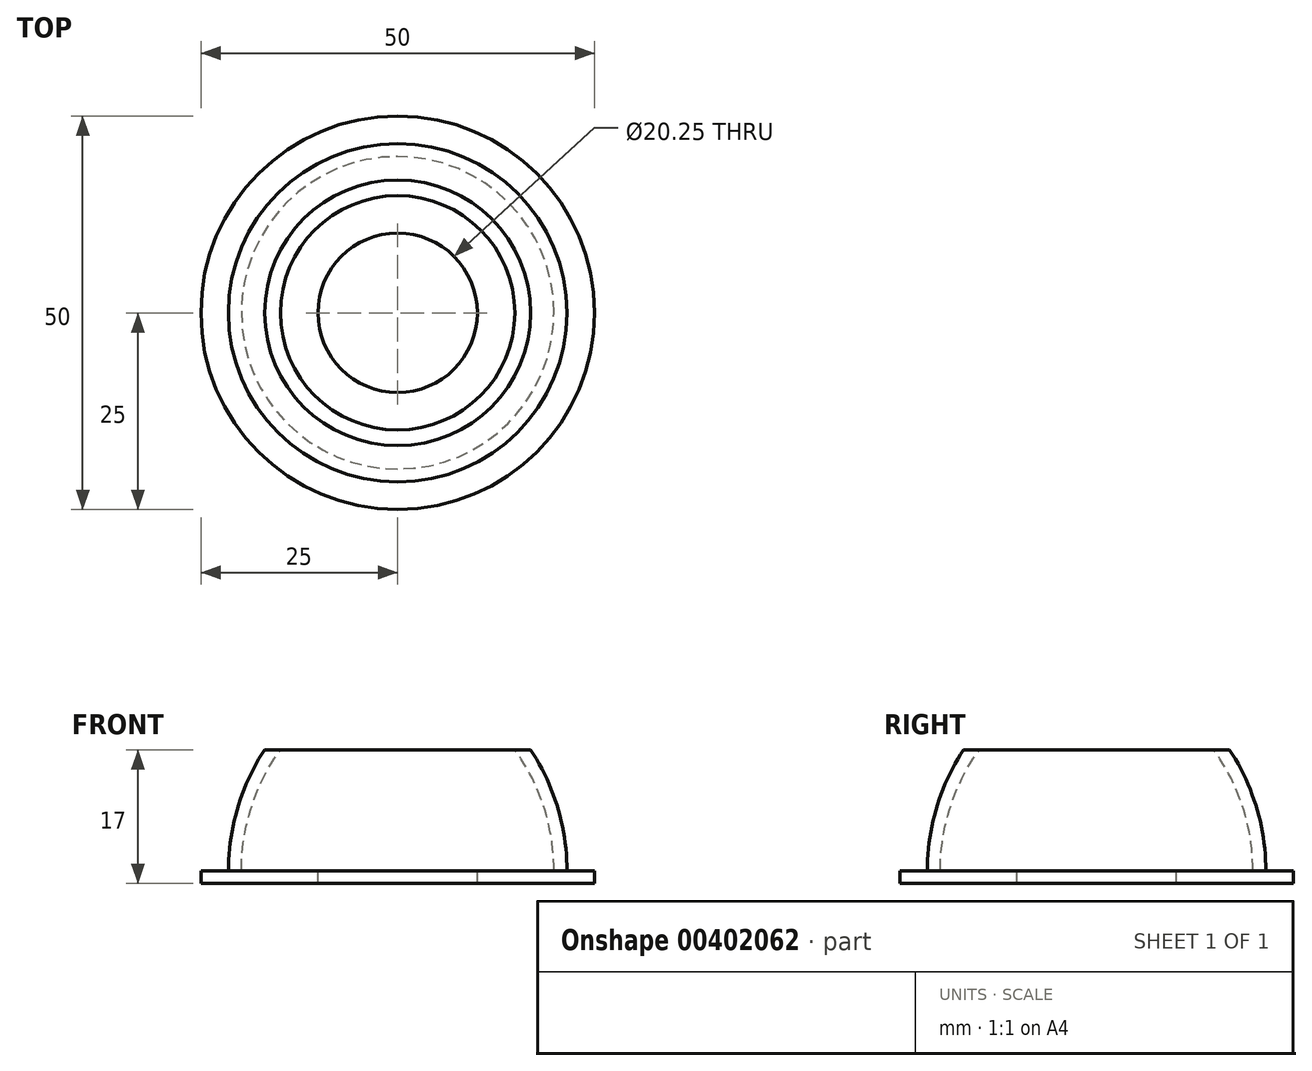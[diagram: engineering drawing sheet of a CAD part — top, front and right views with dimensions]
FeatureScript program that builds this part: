
annotation { "Feature Type Name" : "Feature", "Feature Type Description" : "" }
export const myFeature = defineFeature(function(context is Context, id is Id, definition is map)
    precondition{}
    {
        {
            var Q0;
            Q0=qCreatedBy(makeId("Front.planeOp"),FACE);
            var sketch = newSketch(context, id + "F0", { "sketchPlane" : qUnion([Q0])});
            skLineSegment(sketch, "E0", {"start": v(0, 0) * mm, "end": v(-25, 0) * mm});
            skLineSegment(sketch, "E1", {"start": v(-25, 0) * mm, "end": v(-25, 1.6) * mm});
            skLineSegment(sketch, "E2", {"start": v(-25, 1.6) * mm, "end": v(-21.5, 1.6) * mm});
            skLineSegment(sketch, "E3", {"start": v(-21.5, 1.6) * mm, "end": v(6.5, 1.6) * mm, "construction": true});
            skArc(sketch, "E4", {"start": v(-21.5, 1.6) * mm, "mid": v(-20.32, 9.64) * mm, "end": v(-16.88, 17) * mm});
            skLineSegment(sketch, "E5", {"start": v(-16.88, 17) * mm, "end": v(-14.88, 17) * mm});
            skPoint(sketch, "E6.startSnap0", {"position": v(-20.32, 9.64) * mm});
            skLineSegment(sketch, "E7", {"start": v(-14.88, 17) * mm, "end": v(0, 17) * mm, "construction": true});
            skArc(sketch, "E8", {"start": v(-14.88, 17) * mm, "mid": v(-18.58, 9.7) * mm, "end": v(-19.85, 1.6) * mm});
            skLineSegment(sketch, "E9", {"start": v(-19.85, 1.6) * mm, "end": v(0, 1.6) * mm});
            skLineSegment(sketch, "E10", {"start": v(0, 1.6) * mm, "end": v(0, 0) * mm});
            skLineSegment(sketch, "E11", {"start": v(0, 1.6) * mm, "end": v(0, 48.86) * mm, "construction": true});
            skSolve(sketch);
        }
        {
            var Q0;
            Q0 = qSketchRegion(id + "F0", true);
            var Q1;
            Q1=sQuery(id+"F0.wireOp",EDGE,"E11");
            revolve(context, id + "F1", {"entities" : qUnion([Q0]), "axis" : qUnion([Q1]), "revolveType" : RevolveType.FULL});
        }
        {
            var Q0;
            Q0=makeQuery(id+"F1.opRevolve","SWEPT_FACE",FACE,{"disambiguationData":[OSD([sQuery(id+"F0.wireOp",EDGE,"E9")])]});
            var sketch = newSketch(context, id + "F2", { "sketchPlane" : qUnion([Q0])});
            skCircle(sketch, "E12", {"center": v(0, 0) * mm, "radius": 10.12 * mm});
            skSolve(sketch);
        }
        {
            var Q0;
            Q0 = qSketchRegion(id + "F2", true);
            extrude(context, id + "F3", {"entities" : qUnion([Q0]), "operationType" : NewBodyOperationType.REMOVE, "oppositeDirection" : true, "depth" : 25 * mm});
        }
    });
